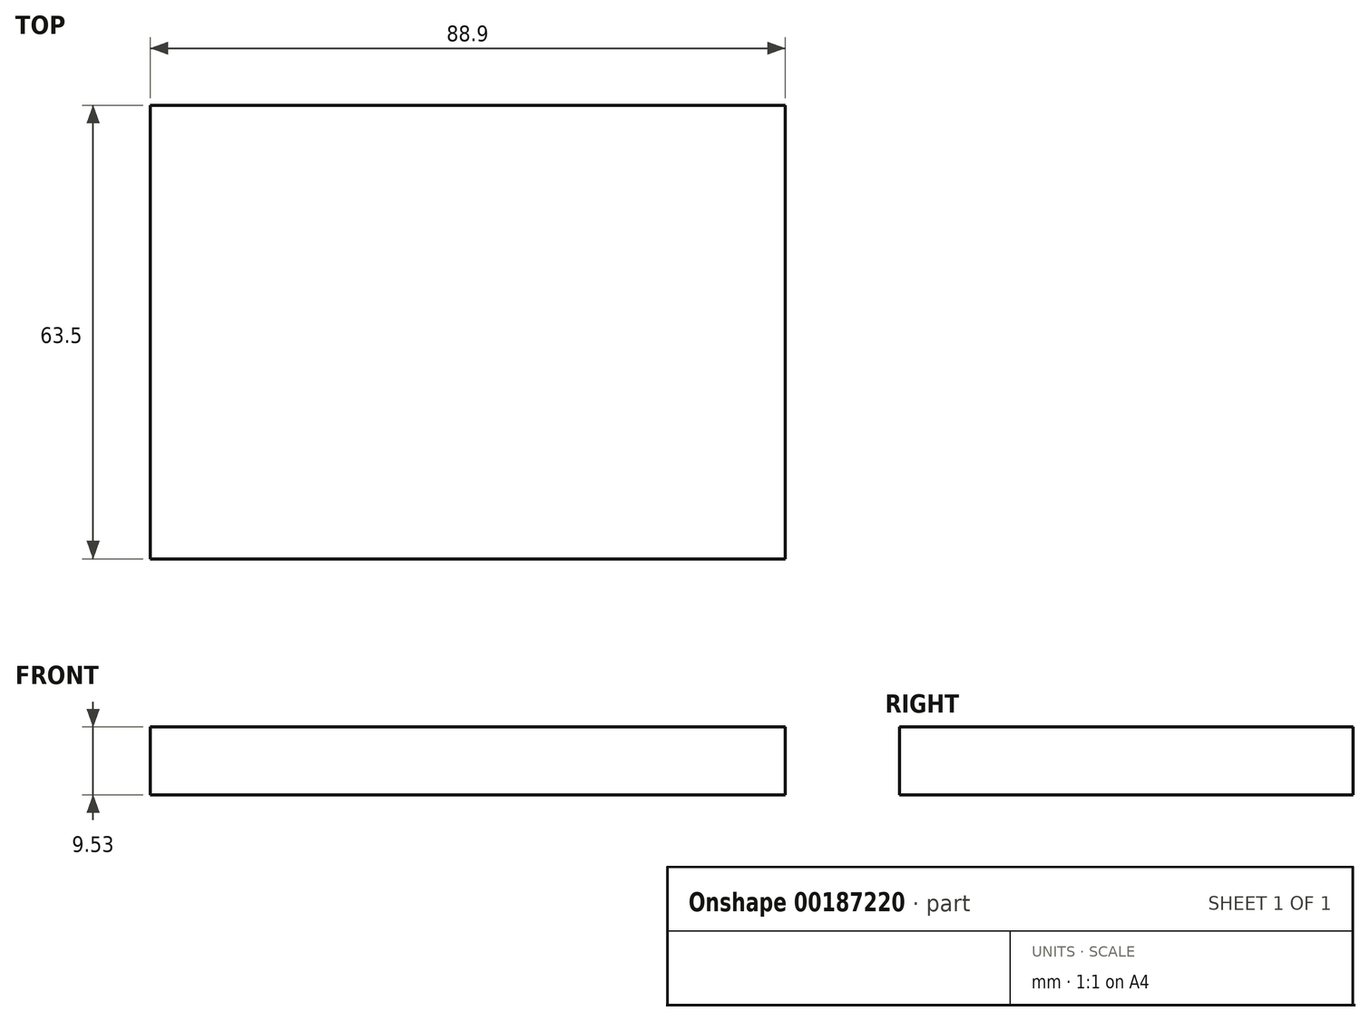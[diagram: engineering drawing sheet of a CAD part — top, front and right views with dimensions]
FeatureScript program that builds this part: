
annotation { "Feature Type Name" : "Feature", "Feature Type Description" : "" }
export const myFeature = defineFeature(function(context is Context, id is Id, definition is map)
    precondition{}
    {
        {
            var Q0;
            Q0=qCreatedBy(makeId("Top.planeOp"),FACE);
            var sketch = newSketch(context, id + "F0", { "sketchPlane" : qUnion([Q0])});
            skLineSegment(sketch, "E0.bottom", {"start": v(0, 0) * mm, "end": v(88.9, 0) * mm});
            skLineSegment(sketch, "E0.top", {"start": v(0, -63.5) * mm, "end": v(88.9, -63.5) * mm});
            skLineSegment(sketch, "E0.left", {"start": v(0, 0) * mm, "end": v(0, -63.5) * mm});
            skLineSegment(sketch, "E0.right", {"start": v(88.9, 0) * mm, "end": v(88.9, -63.5) * mm});
            skSolve(sketch);
        }
        {
            var Q0;
            Q0 = qSketchRegion(id + "F0", true);
            extrude(context, id + "F1", {"entities" : qUnion([Q0]), "depth" : 9.52 * mm});
        }
    });
